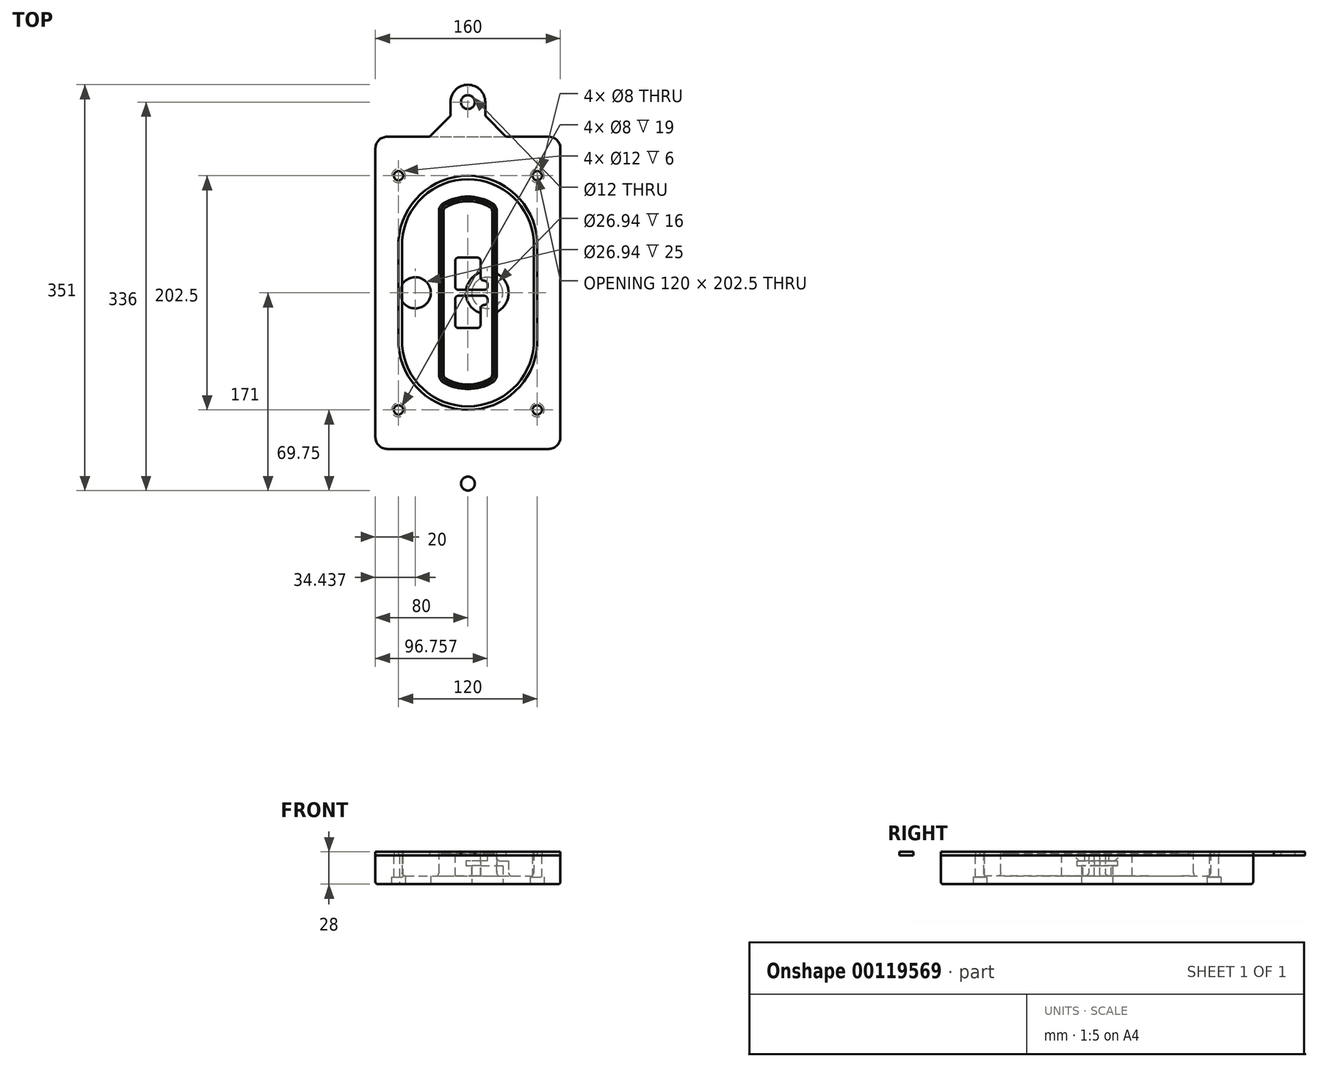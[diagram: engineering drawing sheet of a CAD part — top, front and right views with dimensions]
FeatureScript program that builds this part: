
annotation { "Feature Type Name" : "Feature", "Feature Type Description" : "" }
export const myFeature = defineFeature(function(context is Context, id is Id, definition is map)
    precondition{}
    {
        {
            var Q0;
            Q0=qCreatedBy(makeId("Top.planeOp"),FACE);
            var sketch = newSketch(context, id + "F0", { "sketchPlane" : qUnion([Q0])});
            skPoint(sketch, "E0.rect.middle", {"position": v(0, 0) * mm});
            skLineSegment(sketch, "E1.bottom", {"start": v(-70, -135) * mm, "end": v(70, -135) * mm});
            skLineSegment(sketch, "E1.top", {"start": v(-70, 135) * mm, "end": v(70, 135) * mm});
            skLineSegment(sketch, "E1.left", {"start": v(-80, -125) * mm, "end": v(-80, 125) * mm});
            skLineSegment(sketch, "E1.right", {"start": v(80, -125) * mm, "end": v(80, 125) * mm});
            skLineSegment(sketch, "E2", {"start": v(-80, 135) * mm, "end": v(80, -135) * mm, "construction": true});
            skLineSegment(sketch, "E3", {"start": v(80, 135) * mm, "end": v(-80, -135) * mm, "construction": true});
            skCircle(sketch, "E4", {"center": v(-60, 101.25) * mm, "radius": 4 * mm});
            skCircle(sketch, "E5", {"center": v(60, 101.25) * mm, "radius": 4 * mm});
            skCircle(sketch, "E6", {"center": v(60, -101.25) * mm, "radius": 4 * mm});
            skCircle(sketch, "E7", {"center": v(-60, -101.25) * mm, "radius": 4 * mm});
            skLineSegment(sketch, "E8", {"start": v(-60, 101.25) * mm, "end": v(60, 101.25) * mm, "construction": true});
            skLineSegment(sketch, "E9", {"start": v(60, 101.25) * mm, "end": v(60, -101.25) * mm, "construction": true});
            skLineSegment(sketch, "E10", {"start": v(60, -101.25) * mm, "end": v(-60, -101.25) * mm, "construction": true});
            skLineSegment(sketch, "E11", {"start": v(-60, -101.25) * mm, "end": v(-60, 101.25) * mm, "construction": true});
            skLineSegment(sketch, "E12", {"start": v(-60, 44.66) * mm, "end": v(-60, -44.66) * mm});
            skLineSegment(sketch, "E13", {"start": v(60, 44.66) * mm, "end": v(60, -44.66) * mm});
            skArc(sketch, "E14", {"start": v(59.98, 45.37) * mm, "mid": v(0, 101.25) * mm, "end": v(-59.98, 45.37) * mm});
            skArc(sketch, "E15", {"start": v(-59.98, -45.37) * mm, "mid": v(0, -101.25) * mm, "end": v(59.98, -45.37) * mm});
            skLineSegment(sketch, "E16", {"start": v(-60, 0) * mm, "end": v(60, 0) * mm, "construction": true});
            skPoint(sketch, "E17.visualSharp", {"position": v(-60, -45) * mm});
            skArc(sketch, "E17.filletArc", {"start": v(-60, -44.66) * mm, "mid": v(-60, -45.02) * mm, "end": v(-59.98, -45.37) * mm});
            skPoint(sketch, "E18.visualSharp", {"position": v(-60, 45) * mm});
            skArc(sketch, "E18.filletArc", {"start": v(-59.98, 45.37) * mm, "mid": v(-60, 45.02) * mm, "end": v(-60, 44.66) * mm});
            skPoint(sketch, "E19.visualSharp", {"position": v(60, 45) * mm});
            skArc(sketch, "E19.filletArc", {"start": v(60, 44.66) * mm, "mid": v(60, 45.02) * mm, "end": v(59.98, 45.37) * mm});
            skPoint(sketch, "E20.visualSharp", {"position": v(60, -45) * mm});
            skArc(sketch, "E20.filletArc", {"start": v(59.98, -45.37) * mm, "mid": v(60, -45.02) * mm, "end": v(60, -44.66) * mm});
            skPoint(sketch, "E21.visualSharp", {"position": v(-80, 135) * mm});
            skArc(sketch, "E21.filletArc", {"start": v(-70, 135) * mm, "mid": v(-77.07, 132.07) * mm, "end": v(-80, 125) * mm});
            skPoint(sketch, "E22.visualSharp", {"position": v(80, 135) * mm});
            skArc(sketch, "E22.filletArc", {"start": v(80, 125) * mm, "mid": v(77.07, 132.07) * mm, "end": v(70, 135) * mm});
            skPoint(sketch, "E23.visualSharp", {"position": v(80, -135) * mm});
            skArc(sketch, "E23.filletArc", {"start": v(70, -135) * mm, "mid": v(77.07, -132.07) * mm, "end": v(80, -125) * mm});
            skPoint(sketch, "E24.visualSharp", {"position": v(-80, -135) * mm});
            skArc(sketch, "E24.filletArc", {"start": v(-80, -125) * mm, "mid": v(-77.07, -132.07) * mm, "end": v(-70, -135) * mm});
            skArc(sketch, "E25.0", {"start": v(57, 44.66) * mm, "mid": v(57, 44.9) * mm, "end": v(56.98, 45.16) * mm});
            skLineSegment(sketch, "E25.1", {"start": v(57, 44.66) * mm, "end": v(57, -44.66) * mm});
            skArc(sketch, "E25.2", {"start": v(56.98, -45.16) * mm, "mid": v(57, -44.9) * mm, "end": v(57, -44.66) * mm});
            skArc(sketch, "E25.3", {"start": v(-56.98, -45.16) * mm, "mid": v(0, -98.25) * mm, "end": v(56.98, -45.16) * mm});
            skArc(sketch, "E25.4", {"start": v(-57, -44.66) * mm, "mid": v(-57, -44.9) * mm, "end": v(-56.98, -45.16) * mm});
            skArc(sketch, "E25.5", {"start": v(56.98, 45.16) * mm, "mid": v(0, 98.25) * mm, "end": v(-56.98, 45.16) * mm});
            skLineSegment(sketch, "E25.6", {"start": v(-57, 44.66) * mm, "end": v(-57, -44.66) * mm});
            skArc(sketch, "E25.7", {"start": v(-56.98, 45.16) * mm, "mid": v(-57, 44.9) * mm, "end": v(-57, 44.66) * mm});
            skArc(sketch, "E26.0", {"start": v(-63.97, 45.65) * mm, "mid": v(-64, 45.16) * mm, "end": v(-64, 44.66) * mm});
            skArc(sketch, "E26.1", {"start": v(63.97, 45.65) * mm, "mid": v(0, 105.25) * mm, "end": v(-63.97, 45.65) * mm});
            skArc(sketch, "E26.2", {"start": v(64, 44.66) * mm, "mid": v(64, 45.16) * mm, "end": v(63.97, 45.65) * mm});
            skLineSegment(sketch, "E26.3", {"start": v(64, 44.66) * mm, "end": v(64, -44.66) * mm});
            skArc(sketch, "E26.4", {"start": v(63.97, -45.65) * mm, "mid": v(64, -45.16) * mm, "end": v(64, -44.66) * mm});
            skLineSegment(sketch, "E26.5", {"start": v(-64, 44.66) * mm, "end": v(-64, -44.66) * mm});
            skArc(sketch, "E26.6", {"start": v(-63.97, -45.65) * mm, "mid": v(0, -105.25) * mm, "end": v(63.97, -45.65) * mm});
            skArc(sketch, "E26.7", {"start": v(-64, -44.66) * mm, "mid": v(-64, -45.16) * mm, "end": v(-63.97, -45.65) * mm});
            skSolve(sketch);
        }
        {
            var Q0;
            Q0=makeQuery(id+"F0.imprint","IMPRINT",FACE,{"disambiguationData":[TD([[makeQuery(id+"F0.imprint","IMPRINT",EDGE,{"derivedFrom":sQuery(id+"F0.wireOp",EDGE,"E1.bottom")}),1.0]])]});
            var Q1;
            Q1=makeQuery(id+"F0.imprint","IMPRINT",FACE,{"disambiguationData":[TD([[makeQuery(id+"F0.imprint","IMPRINT",EDGE,{"derivedFrom":sQuery(id+"F0.wireOp",EDGE,"E12")}),1.0]])]});
            var Q2;
            Q2=makeQuery(id+"F0.imprint","IMPRINT",FACE,{"disambiguationData":[TD([[makeQuery(id+"F0.imprint","IMPRINT",EDGE,{"derivedFrom":sQuery(id+"F0.wireOp",EDGE,"E25.0")}),1.0]])]});
            var Q3;
            Q3=makeQuery(id+"F0.imprint","IMPRINT",FACE,{"disambiguationData":[TD([[makeQuery(id+"F0.imprint","IMPRINT",EDGE,{"derivedFrom":sQuery(id+"F0.wireOp",EDGE,"E12")}),-1.0]])]});
            extrude(context, id + "F1", {"entities" : qUnion([Q0, Q1, Q2, Q3]), "oppositeDirection" : true, "depth" : 25 * mm});
        }
        {
            var Q0;
            Q0=makeQuery(id+"F0.imprint","IMPRINT",FACE,{"disambiguationData":[TD([[makeQuery(id+"F0.imprint","IMPRINT",EDGE,{"derivedFrom":sQuery(id+"F0.wireOp",EDGE,"E12")}),1.0]])]});
            extrude(context, id + "F2", {"entities" : qUnion([Q0]), "operationType" : NewBodyOperationType.ADD, "depth" : 3 * mm});
        }
        {
            var Q0;
            Q0=makeQuery(id+"F0.imprint","IMPRINT",FACE,{"disambiguationData":[TD([[makeQuery(id+"F0.imprint","IMPRINT",EDGE,{"derivedFrom":sQuery(id+"F0.wireOp",EDGE,"E25.0")}),1.0]])]});
            extrude(context, id + "F3", {"entities" : qUnion([Q0]), "operationType" : NewBodyOperationType.REMOVE, "oppositeDirection" : true, "depth" : 18 * mm});
        }
        {
            var Q0;
            Q0=makeQuery(id+"F2.opExtrude","CAP_FACE",FACE,{"disambiguationData":[OSD([sQuery(id+"F0.wireOp",EDGE,"E12"),sQuery(id+"F0.wireOp",EDGE,"E13"),sQuery(id+"F0.wireOp",EDGE,"E14"),sQuery(id+"F0.wireOp",EDGE,"E15"),sQuery(id+"F0.wireOp",EDGE,"E17.filletArc"),sQuery(id+"F0.wireOp",EDGE,"E18.filletArc"),sQuery(id+"F0.wireOp",EDGE,"E19.filletArc"),sQuery(id+"F0.wireOp",EDGE,"E20.filletArc"),sQuery(id+"F0.wireOp",EDGE,"E25.0"),sQuery(id+"F0.wireOp",EDGE,"E25.1"),sQuery(id+"F0.wireOp",EDGE,"E25.2"),sQuery(id+"F0.wireOp",EDGE,"E25.3"),sQuery(id+"F0.wireOp",EDGE,"E25.4"),sQuery(id+"F0.wireOp",EDGE,"E25.5"),sQuery(id+"F0.wireOp",EDGE,"E25.6"),sQuery(id+"F0.wireOp",EDGE,"E25.7")])],"isStart":false});
            var sketch = newSketch(context, id + "F4", { "sketchPlane" : qUnion([Q0])});
            skArc(sketch, "E27.0", {"start": v(-20.99, -77.65) * mm, "mid": v(0, -83.25) * mm, "end": v(20.99, -77.65) * mm});
            skArc(sketch, "E28.0", {"start": v(20.99, 77.65) * mm, "mid": v(0, 83.25) * mm, "end": v(-20.99, 77.65) * mm});
            skLineSegment(sketch, "E29", {"start": v(-25, 70.71) * mm, "end": v(-25, -70.71) * mm});
            skLineSegment(sketch, "E30", {"start": v(25, 70.71) * mm, "end": v(25, -70.71) * mm});
            skLineSegment(sketch, "E31", {"start": v(-25, 75.03) * mm, "end": v(25, 75.03) * mm, "construction": true});
            skLineSegment(sketch, "E32", {"start": v(-25, -75.03) * mm, "end": v(25, -75.03) * mm, "construction": true});
            skPoint(sketch, "E33.visualSharp", {"position": v(-25, 75.03) * mm});
            skArc(sketch, "E33.filletArc", {"start": v(-20.99, 77.65) * mm, "mid": v(-23.92, 74.72) * mm, "end": v(-25, 70.71) * mm});
            skPoint(sketch, "E34.visualSharp", {"position": v(25, 75.03) * mm});
            skArc(sketch, "E34.filletArc", {"start": v(25, 70.71) * mm, "mid": v(23.92, 74.72) * mm, "end": v(20.99, 77.65) * mm});
            skPoint(sketch, "E35.visualSharp", {"position": v(25, -75.03) * mm});
            skArc(sketch, "E35.filletArc", {"start": v(20.99, -77.65) * mm, "mid": v(23.92, -74.72) * mm, "end": v(25, -70.71) * mm});
            skPoint(sketch, "E36.visualSharp", {"position": v(-25, -75.03) * mm});
            skArc(sketch, "E36.filletArc", {"start": v(-25, -70.71) * mm, "mid": v(-23.92, -74.72) * mm, "end": v(-20.99, -77.65) * mm});
            skArc(sketch, "E37.0", {"start": v(56.98, 45.16) * mm, "mid": v(0, 98.25) * mm, "end": v(-56.98, 45.16) * mm});
            skArc(sketch, "E37.1", {"start": v(-56.98, 45.16) * mm, "mid": v(-57, 44.9) * mm, "end": v(-57, 44.66) * mm});
            skLineSegment(sketch, "E37.2", {"start": v(-57, 44.66) * mm, "end": v(-57, -44.66) * mm});
            skArc(sketch, "E37.3", {"start": v(-57, -44.66) * mm, "mid": v(-57, -44.9) * mm, "end": v(-56.98, -45.16) * mm});
            skArc(sketch, "E37.4", {"start": v(-56.98, -45.16) * mm, "mid": v(0, -98.25) * mm, "end": v(56.98, -45.16) * mm});
            skArc(sketch, "E37.5", {"start": v(56.98, -45.16) * mm, "mid": v(57, -44.9) * mm, "end": v(57, -44.66) * mm});
            skLineSegment(sketch, "E37.6", {"start": v(57, 44.66) * mm, "end": v(57, -44.66) * mm});
            skArc(sketch, "E37.7", {"start": v(57, 44.66) * mm, "mid": v(57, 44.9) * mm, "end": v(56.98, 45.16) * mm});
            skLineSegment(sketch, "E38.0", {"start": v(23, 70.71) * mm, "end": v(23, -70.71) * mm});
            skArc(sketch, "E38.1", {"start": v(19.99, -75.92) * mm, "mid": v(22.2, -73.72) * mm, "end": v(23, -70.71) * mm});
            skArc(sketch, "E38.2", {"start": v(-19.99, -75.92) * mm, "mid": v(0, -81.25) * mm, "end": v(19.99, -75.92) * mm});
            skArc(sketch, "E38.3", {"start": v(-23, -70.71) * mm, "mid": v(-22.2, -73.72) * mm, "end": v(-19.99, -75.92) * mm});
            skLineSegment(sketch, "E38.4", {"start": v(-23, 70.71) * mm, "end": v(-23, -70.71) * mm});
            skArc(sketch, "E38.5", {"start": v(23, 70.71) * mm, "mid": v(22.2, 73.72) * mm, "end": v(19.99, 75.92) * mm});
            skArc(sketch, "E38.6", {"start": v(-19.99, 75.92) * mm, "mid": v(-22.2, 73.72) * mm, "end": v(-23, 70.71) * mm});
            skArc(sketch, "E38.7", {"start": v(19.99, 75.92) * mm, "mid": v(0, 81.25) * mm, "end": v(-19.99, 75.92) * mm});
            skArc(sketch, "E39.0", {"start": v(21, 70.71) * mm, "mid": v(20.46, 72.72) * mm, "end": v(19, 74.18) * mm});
            skLineSegment(sketch, "E39.1", {"start": v(21, 70.71) * mm, "end": v(21, -70.71) * mm});
            skArc(sketch, "E39.2", {"start": v(19, -74.18) * mm, "mid": v(20.46, -72.72) * mm, "end": v(21, -70.71) * mm});
            skArc(sketch, "E39.3", {"start": v(-19, -74.18) * mm, "mid": v(0, -79.25) * mm, "end": v(19, -74.18) * mm});
            skArc(sketch, "E39.4", {"start": v(-21, -70.71) * mm, "mid": v(-20.46, -72.72) * mm, "end": v(-19, -74.18) * mm});
            skArc(sketch, "E39.5", {"start": v(19, 74.18) * mm, "mid": v(0, 79.25) * mm, "end": v(-19, 74.18) * mm});
            skLineSegment(sketch, "E39.6", {"start": v(-21, 70.71) * mm, "end": v(-21, -70.71) * mm});
            skArc(sketch, "E39.7", {"start": v(-19, 74.18) * mm, "mid": v(-20.46, 72.72) * mm, "end": v(-21, 70.71) * mm});
            skLineSegment(sketch, "E40", {"start": v(-25, 0) * mm, "end": v(25, 0) * mm, "construction": true});
            skLineSegment(sketch, "E41", {"start": v(-11, 5.5) * mm, "end": v(-11, 27.5) * mm});
            skLineSegment(sketch, "E42", {"start": v(-8, 30.5) * mm, "end": v(8, 30.5) * mm});
            skLineSegment(sketch, "E43", {"start": v(11, 27.5) * mm, "end": v(11, 13.5) * mm});
            skLineSegment(sketch, "E44", {"start": v(14, 10.5) * mm, "end": v(14, 10.5) * mm});
            skLineSegment(sketch, "E45", {"start": v(17, 7.5) * mm, "end": v(17, 5.5) * mm});
            skLineSegment(sketch, "E46", {"start": v(14, 2.5) * mm, "end": v(-8, 2.5) * mm});
            skPoint(sketch, "E47.visualSharp", {"position": v(-11, 30.5) * mm});
            skArc(sketch, "E47.filletArc", {"start": v(-8, 30.5) * mm, "mid": v(-10.12, 29.62) * mm, "end": v(-11, 27.5) * mm});
            skPoint(sketch, "E48.visualSharp", {"position": v(11, 30.5) * mm});
            skArc(sketch, "E48.filletArc", {"start": v(11, 27.5) * mm, "mid": v(10.12, 29.62) * mm, "end": v(8, 30.5) * mm});
            skPoint(sketch, "E49.visualSharp", {"position": v(11, 10.5) * mm});
            skArc(sketch, "E49.filletArc", {"start": v(11, 13.5) * mm, "mid": v(11.88, 11.38) * mm, "end": v(14, 10.5) * mm});
            skPoint(sketch, "E50.visualSharp", {"position": v(17, 10.5) * mm});
            skArc(sketch, "E50.filletArc", {"start": v(17, 7.5) * mm, "mid": v(16.12, 9.62) * mm, "end": v(14, 10.5) * mm});
            skPoint(sketch, "E51.visualSharp", {"position": v(17, 2.5) * mm});
            skArc(sketch, "E51.filletArc", {"start": v(14, 2.5) * mm, "mid": v(16.12, 3.38) * mm, "end": v(17, 5.5) * mm});
            skPoint(sketch, "E52.visualSharp", {"position": v(-11, 2.5) * mm});
            skArc(sketch, "E52.filletArc", {"start": v(-11, 5.5) * mm, "mid": v(-10.12, 3.38) * mm, "end": v(-8, 2.5) * mm});
            skLineSegment(sketch, "E53.0.MirrorCS", {"start": v(14, -2.5) * mm, "end": v(-8, -2.5) * mm});
            skArc(sketch, "E54.0.MirrorCS", {"start": v(-11, -5.5) * mm, "mid": v(-10.12, -3.38) * mm, "end": v(-8, -2.5) * mm});
            skLineSegment(sketch, "E55.0.MirrorCS", {"start": v(-11, -5.5) * mm, "end": v(-11, -27.5) * mm});
            skArc(sketch, "E56.0.MirrorCS", {"start": v(-8, -30.5) * mm, "mid": v(-10.12, -29.62) * mm, "end": v(-11, -27.5) * mm});
            skLineSegment(sketch, "E57.0.MirrorCS", {"start": v(-8, -30.5) * mm, "end": v(8, -30.5) * mm});
            skArc(sketch, "E58.0.MirrorCS", {"start": v(11, -27.5) * mm, "mid": v(10.12, -29.62) * mm, "end": v(8, -30.5) * mm});
            skLineSegment(sketch, "E59.0.MirrorCS", {"start": v(11, -27.5) * mm, "end": v(11, -13.5) * mm});
            skArc(sketch, "E60.0.MirrorCS", {"start": v(11, -13.5) * mm, "mid": v(11.88, -11.38) * mm, "end": v(14, -10.5) * mm});
            skArc(sketch, "E61.0.MirrorCS", {"start": v(17, -7.5) * mm, "mid": v(16.12, -9.62) * mm, "end": v(14, -10.5) * mm});
            skLineSegment(sketch, "E62.0.MirrorCS", {"start": v(17, -7.5) * mm, "end": v(17, -5.5) * mm});
            skArc(sketch, "E63.0.MirrorCS", {"start": v(14, -2.5) * mm, "mid": v(16.12, -3.38) * mm, "end": v(17, -5.5) * mm});
            skSolve(sketch);
        }
        {
            var Q0;
            Q0=makeQuery(id+"F4.imprint","IMPRINT",FACE,{"disambiguationData":[TD([[makeQuery(id+"F4.imprint","IMPRINT",EDGE,{"derivedFrom":sQuery(id+"F4.wireOp",EDGE,"E27.0")}),1.0]])]});
            var Q1;
            Q1=makeQuery(id+"F4.imprint","IMPRINT",FACE,{"disambiguationData":[TD([[makeQuery(id+"F4.imprint","IMPRINT",EDGE,{"derivedFrom":sQuery(id+"F4.wireOp",EDGE,"E38.0")}),-1.0]])]});
            var Q2;
            Q2=makeQuery(id+"F4.imprint","IMPRINT",FACE,{"disambiguationData":[TD([[makeQuery(id+"F4.imprint","IMPRINT",EDGE,{"derivedFrom":sQuery(id+"F4.wireOp",EDGE,"E39.0")}),1.0]])]});
            extrude(context, id + "F5", {"entities" : qUnion([Q0, Q1, Q2]), "operationType" : NewBodyOperationType.ADD, "endBound" : BoundingType.UP_TO_NEXT, "oppositeDirection" : true, "depth" : 25 * mm});
        }
        {
            var Q0;
            Q0=makeQuery(id+"F4.imprint","IMPRINT",FACE,{"disambiguationData":[TD([[makeQuery(id+"F4.imprint","IMPRINT",EDGE,{"derivedFrom":sQuery(id+"F4.wireOp",EDGE,"E38.0")}),-1.0]])]});
            extrude(context, id + "F6", {"entities" : qUnion([Q0]), "operationType" : NewBodyOperationType.REMOVE, "oppositeDirection" : true, "depth" : 2 * mm});
        }
        {
            var Q0;
            Q0=makeQuery(id+"F1.opExtrude","CAP_FACE",FACE,{"disambiguationData":[OSD([sQuery(id+"F0.wireOp",EDGE,"E1.bottom"),sQuery(id+"F0.wireOp",EDGE,"E1.top"),sQuery(id+"F0.wireOp",EDGE,"E1.left"),sQuery(id+"F0.wireOp",EDGE,"E1.right"),sQuery(id+"F0.wireOp",EDGE,"E4"),sQuery(id+"F0.wireOp",EDGE,"E5"),sQuery(id+"F0.wireOp",EDGE,"E6"),sQuery(id+"F0.wireOp",EDGE,"E7"),sQuery(id+"F0.wireOp",EDGE,"E21.filletArc"),sQuery(id+"F0.wireOp",EDGE,"E22.filletArc"),sQuery(id+"F0.wireOp",EDGE,"E23.filletArc"),sQuery(id+"F0.wireOp",EDGE,"E24.filletArc")])],"isStart":false});
            var sketch = newSketch(context, id + "F7", { "sketchPlane" : qUnion([Q0])});
            skCircle(sketch, "E64", {"center": v(16.76, 0) * mm, "radius": 13.47 * mm});
            skCircle(sketch, "E65", {"center": v(-45.56, 0) * mm, "radius": 13.47 * mm});
            skLineSegment(sketch, "E66", {"start": v(80, 0) * mm, "end": v(-80, 0) * mm});
            skCircle(sketch, "E67", {"center": v(16.76, 0) * mm, "radius": 18.47 * mm});
            skCircle(sketch, "E68", {"center": v(60, -101.25) * mm, "radius": 6 * mm});
            skCircle(sketch, "E69", {"center": v(-60, -101.25) * mm, "radius": 6 * mm});
            skCircle(sketch, "E70", {"center": v(-60, 101.25) * mm, "radius": 6 * mm});
            skCircle(sketch, "E71", {"center": v(60, 101.25) * mm, "radius": 6 * mm});
            skSolve(sketch);
        }
        {
            var Q0;
            {var subQ1=sQuery(id+"F7.wireOp",EDGE,"E66");var subQ4=sQuery(id+"F7.wireOp",EDGE,"E64");var subQ6=makeQuery(id+"F7.imprint","INTERSECT",VERTEX,{"disambiguationData":[OD(0.0)],"derivedFrom":[subQ4,subQ1]});Q0=makeQuery(id+"F7.imprint","IMPRINT",FACE,{"disambiguationData":[TD([[makeQuery(id+"F7.imprint","IMPRINT",EDGE,{"disambiguationData":[TD([[subQ6,-1.0]])],"derivedFrom":subQ4}),-1.0]])]});}
            var Q1;
            {var subQ0=sQuery(id+"F7.wireOp",EDGE,"E66");var subQ1=sQuery(id+"F7.wireOp",EDGE,"E64");var subQ3=makeQuery(id+"F7.imprint","INTERSECT",VERTEX,{"disambiguationData":[OD(0.0)],"derivedFrom":[subQ1,subQ0]});Q1=makeQuery(id+"F7.imprint","IMPRINT",FACE,{"disambiguationData":[TD([[makeQuery(id+"F7.imprint","IMPRINT",EDGE,{"disambiguationData":[TD([[subQ3,-1.0]])],"derivedFrom":subQ1}),1.0]])]});}
            var Q2;
            {var subQ0=sQuery(id+"F7.wireOp",EDGE,"E66");var subQ1=sQuery(id+"F7.wireOp",EDGE,"E64");var subQ3=makeQuery(id+"F7.imprint","INTERSECT",VERTEX,{"disambiguationData":[OD(0.0)],"derivedFrom":[subQ1,subQ0]});Q2=makeQuery(id+"F7.imprint","IMPRINT",FACE,{"disambiguationData":[TD([[makeQuery(id+"F7.imprint","IMPRINT",EDGE,{"disambiguationData":[TD([[subQ3,1.0]])],"derivedFrom":subQ1}),1.0]])]});}
            var Q3;
            {var subQ1=sQuery(id+"F7.wireOp",EDGE,"E66");var subQ4=sQuery(id+"F7.wireOp",EDGE,"E64");var subQ6=makeQuery(id+"F7.imprint","INTERSECT",VERTEX,{"disambiguationData":[OD(0.0)],"derivedFrom":[subQ4,subQ1]});Q3=makeQuery(id+"F7.imprint","IMPRINT",FACE,{"disambiguationData":[TD([[makeQuery(id+"F7.imprint","IMPRINT",EDGE,{"disambiguationData":[TD([[subQ6,1.0]])],"derivedFrom":subQ4}),-1.0]])]});}
            extrude(context, id + "F8", {"entities" : qUnion([Q0, Q1, Q2, Q3]), "operationType" : NewBodyOperationType.ADD, "oppositeDirection" : true, "depth" : 20 * mm});
        }
        {
            var Q0;
            {var subQ0=sQuery(id+"F7.wireOp",EDGE,"E66");var subQ1=sQuery(id+"F7.wireOp",EDGE,"E64");var subQ3=makeQuery(id+"F7.imprint","INTERSECT",VERTEX,{"disambiguationData":[OD(0.0)],"derivedFrom":[subQ1,subQ0]});Q0=makeQuery(id+"F7.imprint","IMPRINT",FACE,{"disambiguationData":[TD([[makeQuery(id+"F7.imprint","IMPRINT",EDGE,{"disambiguationData":[TD([[subQ3,-1.0]])],"derivedFrom":subQ1}),1.0]])]});}
            var Q1;
            {var subQ0=sQuery(id+"F7.wireOp",EDGE,"E66");var subQ1=sQuery(id+"F7.wireOp",EDGE,"E64");var subQ3=makeQuery(id+"F7.imprint","INTERSECT",VERTEX,{"disambiguationData":[OD(0.0)],"derivedFrom":[subQ1,subQ0]});Q1=makeQuery(id+"F7.imprint","IMPRINT",FACE,{"disambiguationData":[TD([[makeQuery(id+"F7.imprint","IMPRINT",EDGE,{"disambiguationData":[TD([[subQ3,1.0]])],"derivedFrom":subQ1}),1.0]])]});}
            extrude(context, id + "F9", {"entities" : qUnion([Q0, Q1]), "operationType" : NewBodyOperationType.REMOVE, "oppositeDirection" : true, "depth" : 16 * mm});
        }
        {
            var Q0;
            {var subQ0=sQuery(id+"F7.wireOp",EDGE,"E66");var subQ1=sQuery(id+"F7.wireOp",EDGE,"E65");var subQ3=makeQuery(id+"F7.imprint","INTERSECT",VERTEX,{"disambiguationData":[OD(0.0)],"derivedFrom":[subQ1,subQ0]});Q0=makeQuery(id+"F7.imprint","IMPRINT",FACE,{"disambiguationData":[TD([[makeQuery(id+"F7.imprint","IMPRINT",EDGE,{"disambiguationData":[TD([[subQ3,-1.0]])],"derivedFrom":subQ1}),1.0]])]});}
            var Q1;
            {var subQ0=sQuery(id+"F7.wireOp",EDGE,"E66");var subQ1=sQuery(id+"F7.wireOp",EDGE,"E65");var subQ3=makeQuery(id+"F7.imprint","INTERSECT",VERTEX,{"disambiguationData":[OD(0.0)],"derivedFrom":[subQ1,subQ0]});Q1=makeQuery(id+"F7.imprint","IMPRINT",FACE,{"disambiguationData":[TD([[makeQuery(id+"F7.imprint","IMPRINT",EDGE,{"disambiguationData":[TD([[subQ3,1.0]])],"derivedFrom":subQ1}),1.0]])]});}
            extrude(context, id + "F10", {"entities" : qUnion([Q0, Q1]), "operationType" : NewBodyOperationType.REMOVE, "oppositeDirection" : true, "depth" : 25 * mm});
        }
        {
            var Q0;
            Q0=makeQuery(id+"F7.imprint","IMPRINT",FACE,{"disambiguationData":[TD([[makeQuery(id+"F7.imprint","IMPRINT",EDGE,{"derivedFrom":sQuery(id+"F7.wireOp",EDGE,"E68")}),1.0]])]});
            var Q1;
            Q1=makeQuery(id+"F7.imprint","IMPRINT",FACE,{"disambiguationData":[TD([[makeQuery(id+"F7.imprint","IMPRINT",EDGE,{"derivedFrom":makeQuery(id+"F1.opExtrude","CAP_EDGE",EDGE,{"disambiguationData":[OSD([sQuery(id+"F0.wireOp",EDGE,"E5")])],"isStart":false})}),-1.0]])]});
            var Q2;
            Q2=makeQuery(id+"F7.imprint","IMPRINT",FACE,{"disambiguationData":[TD([[makeQuery(id+"F7.imprint","IMPRINT",EDGE,{"derivedFrom":sQuery(id+"F7.wireOp",EDGE,"E69")}),1.0]])]});
            var Q3;
            Q3=makeQuery(id+"F7.imprint","IMPRINT",FACE,{"disambiguationData":[TD([[makeQuery(id+"F7.imprint","IMPRINT",EDGE,{"derivedFrom":makeQuery(id+"F1.opExtrude","CAP_EDGE",EDGE,{"disambiguationData":[OSD([sQuery(id+"F0.wireOp",EDGE,"E4")])],"isStart":false})}),-1.0]])]});
            var Q4;
            Q4=makeQuery(id+"F7.imprint","IMPRINT",FACE,{"disambiguationData":[TD([[makeQuery(id+"F7.imprint","IMPRINT",EDGE,{"derivedFrom":sQuery(id+"F7.wireOp",EDGE,"E70")}),1.0]])]});
            var Q5;
            Q5=makeQuery(id+"F7.imprint","IMPRINT",FACE,{"disambiguationData":[TD([[makeQuery(id+"F7.imprint","IMPRINT",EDGE,{"derivedFrom":makeQuery(id+"F1.opExtrude","CAP_EDGE",EDGE,{"disambiguationData":[OSD([sQuery(id+"F0.wireOp",EDGE,"E7")])],"isStart":false})}),-1.0]])]});
            var Q6;
            Q6=makeQuery(id+"F7.imprint","IMPRINT",FACE,{"disambiguationData":[TD([[makeQuery(id+"F7.imprint","IMPRINT",EDGE,{"derivedFrom":sQuery(id+"F7.wireOp",EDGE,"E71")}),1.0]])]});
            var Q7;
            Q7=makeQuery(id+"F7.imprint","IMPRINT",FACE,{"disambiguationData":[TD([[makeQuery(id+"F7.imprint","IMPRINT",EDGE,{"derivedFrom":makeQuery(id+"F1.opExtrude","CAP_EDGE",EDGE,{"disambiguationData":[OSD([sQuery(id+"F0.wireOp",EDGE,"E6")])],"isStart":false})}),-1.0]])]});
            extrude(context, id + "F11", {"entities" : qUnion([Q0, Q1, Q2, Q3, Q4, Q5, Q6, Q7]), "operationType" : NewBodyOperationType.REMOVE, "oppositeDirection" : true, "depth" : 6 * mm});
        }
        {
            var Q0;
            Q0=makeQuery(id+"F9.boolean.opBoolean","COPY",FACE,{"derivedFrom":makeQuery(id+"F9.opExtrude","CAP_FACE",FACE,{"disambiguationData":[OSD([sQuery(id+"F7.wireOp",EDGE,"E64")])],"isStart":false})});
            var sketch = newSketch(context, id + "F12", { "sketchPlane" : qUnion([Q0])});
            skArc(sketch, "E72.0", {"start": v(11, 17.55) * mm, "mid": v(2.57, 11.82) * mm, "end": v(-1.54, 2.5) * mm});
            skArc(sketch, "E72.1", {"start": v(-1.54, -2.5) * mm, "mid": v(2.57, -11.82) * mm, "end": v(11, -17.55) * mm});
            skLineSegment(sketch, "E73", {"start": v(-1.54, -2.5) * mm, "end": v(14, -2.5) * mm});
            skLineSegment(sketch, "E74.0", {"start": v(14, 2.5) * mm, "end": v(-1.54, 2.5) * mm});
            skArc(sketch, "E74.1", {"start": v(14, 2.5) * mm, "mid": v(16.12, 3.38) * mm, "end": v(17, 5.5) * mm});
            skLineSegment(sketch, "E74.2", {"start": v(17, 7.5) * mm, "end": v(17, 5.5) * mm});
            skArc(sketch, "E74.3", {"start": v(17, 7.5) * mm, "mid": v(16.12, 9.62) * mm, "end": v(14, 10.5) * mm});
            skArc(sketch, "E74.4", {"start": v(11, 13.5) * mm, "mid": v(11.88, 11.38) * mm, "end": v(14, 10.5) * mm});
            skLineSegment(sketch, "E74.5", {"start": v(11, 17.55) * mm, "end": v(11, 13.5) * mm});
            skLineSegment(sketch, "E74.7", {"start": v(14, -2.5) * mm, "end": v(-1.54, -2.5) * mm});
            skArc(sketch, "E74.8", {"start": v(14, -2.5) * mm, "mid": v(16.12, -3.38) * mm, "end": v(17, -5.5) * mm});
            skLineSegment(sketch, "E74.9", {"start": v(17, -7.5) * mm, "end": v(17, -5.5) * mm});
            skArc(sketch, "E74.10", {"start": v(17, -7.5) * mm, "mid": v(16.12, -9.62) * mm, "end": v(14, -10.5) * mm});
            skArc(sketch, "E74.11", {"start": v(11, -13.5) * mm, "mid": v(11.88, -11.38) * mm, "end": v(14, -10.5) * mm});
            skLineSegment(sketch, "E74.12", {"start": v(11, -17.55) * mm, "end": v(11, -13.5) * mm});
            skPoint(sketch, "E75.orphan", {"position": v(11, -27.5) * mm});
            skPoint(sketch, "E76.orphan", {"position": v(-8, -2.5) * mm});
            skPoint(sketch, "E77.orphan", {"position": v(-8, 2.5) * mm});
            skPoint(sketch, "E78.orphan", {"position": v(11, 27.5) * mm});
            skSolve(sketch);
        }
        {
            var Q0;
            {var subQ7=sQuery(id+"F12.wireOp",EDGE,"E72.0");var subQ14=sQuery(id+"F12.wireOp",EDGE,"E72.1");var subQ16=sQuery(id+"F12.wireOp",EDGE,"E74.1");var subQ18=sQuery(id+"F12.wireOp",EDGE,"E74.8");Q0=qUnion([makeQuery(id+"F12.imprint","IMPRINT",FACE,{"disambiguationData":[TD([[makeQuery(id+"F12.imprint","IMPRINT",EDGE,{"derivedFrom":subQ7}),1.0]])]}),makeQuery(id+"F12.imprint","IMPRINT",FACE,{"disambiguationData":[TD([[makeQuery(id+"F12.imprint","IMPRINT",EDGE,{"derivedFrom":subQ14}),1.0]])]}),makeQuery(id+"F12.imprint","IMPRINT",FACE,{"disambiguationData":[TD([[makeQuery(id+"F12.imprint","IMPRINT",EDGE,{"derivedFrom":subQ16}),1.0]])]}),makeQuery(id+"F12.imprint","IMPRINT",FACE,{"disambiguationData":[TD([[makeQuery(id+"F12.imprint","IMPRINT",EDGE,{"derivedFrom":subQ18}),-1.0]])]})]);}
            var Q1;
            Q1=makeQuery(id+"F5.boolean.opBoolean","SPLIT",FACE,{"disambiguationData":[TD([makeQuery(id+"F5.opExtrude","SWEPT_FACE",FACE,{"disambiguationData":[OSD([sQuery(id+"F4.wireOp",EDGE,"E41")])]})])],"derivedFrom":makeQuery(id+"F3.boolean.opBoolean","COPY",FACE,{"derivedFrom":makeQuery(id+"F3.opExtrude","CAP_FACE",FACE,{"disambiguationData":[OSD([sQuery(id+"F0.wireOp",EDGE,"E25.0"),sQuery(id+"F0.wireOp",EDGE,"E25.1"),sQuery(id+"F0.wireOp",EDGE,"E25.2"),sQuery(id+"F0.wireOp",EDGE,"E25.3"),sQuery(id+"F0.wireOp",EDGE,"E25.4"),sQuery(id+"F0.wireOp",EDGE,"E25.5"),sQuery(id+"F0.wireOp",EDGE,"E25.6"),sQuery(id+"F0.wireOp",EDGE,"E25.7")])],"isStart":false})})});
            extrude(context, id + "F13", {"entities" : qUnion([Q0]), "operationType" : NewBodyOperationType.REMOVE, "endBound" : BoundingType.UP_TO_SURFACE, "endBoundEntityFace" : qUnion([Q1]), "depth" : 25 * mm});
        }
        {
            var Q0;
            Q0=makeQuery(id+"F3.boolean.opBoolean","COPY",EDGE,{"derivedFrom":makeQuery(id+"F3.opExtrude","CAP_EDGE",EDGE,{"disambiguationData":[OSD([sQuery(id+"F0.wireOp",EDGE,"E25.6")])],"isStart":false})});
            var Q1;
            Q1=makeQuery(id+"F8.boolean.opBoolean","INTERSECT",EDGE,{"derivedFrom":[makeQuery(id+"F5.opExtrude","SWEPT_FACE",FACE,{"disambiguationData":[OSD([sQuery(id+"F4.wireOp",EDGE,"E30")])]}),makeQuery(id+"F8.opExtrude","CAP_FACE",FACE,{"disambiguationData":[OSD([sQuery(id+"F7.wireOp",EDGE,"E67")])],"isStart":false})]});
            var Q2;
            Q2=makeQuery(id+"F8.boolean.opBoolean","INTERSECT",EDGE,{"disambiguationData":[OD(1.0)],"derivedFrom":[makeQuery(id+"F5.opExtrude","SWEPT_FACE",FACE,{"disambiguationData":[OSD([sQuery(id+"F4.wireOp",EDGE,"E30")])]}),makeQuery(id+"F8.opExtrude","SWEPT_FACE",FACE,{"disambiguationData":[OSD([sQuery(id+"F7.wireOp",EDGE,"E67")])]})]});
            var Q3;
            {var subQ0=sQuery(id+"F4.wireOp",EDGE,"E30");Q3=makeQuery(id+"F8.boolean.opBoolean","SPLIT",EDGE,{"disambiguationData":[TD([makeQuery(id+"F5.opExtrude","SWEPT_FACE",FACE,{"disambiguationData":[OSD([sQuery(id+"F4.wireOp",EDGE,"E35.filletArc")])]})])],"derivedFrom":makeQuery(id+"F5.opExtrude","CAP_EDGE",EDGE,{"disambiguationData":[OSD([subQ0])],"isStart":false})});}
            var Q4;
            {var subQ0=sQuery(id+"F0.wireOp",EDGE,"E25.7");var subQ1=sQuery(id+"F0.wireOp",EDGE,"E25.1");var subQ2=sQuery(id+"F0.wireOp",EDGE,"E25.6");var subQ3=sQuery(id+"F0.wireOp",EDGE,"E25.5");var subQ4=sQuery(id+"F0.wireOp",EDGE,"E25.4");var subQ5=sQuery(id+"F0.wireOp",EDGE,"E25.0");var subQ6=sQuery(id+"F0.wireOp",EDGE,"E25.2");var subQ7=sQuery(id+"F0.wireOp",EDGE,"E25.3");Q4=makeQuery(id+"F8.boolean.opBoolean","INTERSECT",EDGE,{"derivedFrom":[makeQuery(id+"F5.boolean.opBoolean","SPLIT",FACE,{"disambiguationData":[TD([makeQuery(id+"F2.opExtrude","SWEPT_FACE",FACE,{"disambiguationData":[OSD([subQ5])]})])],"derivedFrom":makeQuery(id+"F3.boolean.opBoolean","COPY",FACE,{"derivedFrom":makeQuery(id+"F3.opExtrude","CAP_FACE",FACE,{"disambiguationData":[OSD([subQ5,subQ1,subQ6,subQ7,subQ4,subQ3,subQ2,subQ0])],"isStart":false})})}),makeQuery(id+"F8.opExtrude","SWEPT_FACE",FACE,{"disambiguationData":[OSD([sQuery(id+"F7.wireOp",EDGE,"E67")])]})]});}
            var Q5;
            Q5=makeQuery(id+"F8.boolean.opBoolean","INTERSECT",EDGE,{"disambiguationData":[OD(0.0)],"derivedFrom":[makeQuery(id+"F5.opExtrude","SWEPT_FACE",FACE,{"disambiguationData":[OSD([sQuery(id+"F4.wireOp",EDGE,"E30")])]}),makeQuery(id+"F8.opExtrude","SWEPT_FACE",FACE,{"disambiguationData":[OSD([sQuery(id+"F7.wireOp",EDGE,"E67")])]})]});
            fillet(context, id + "F14", {"entities" : qUnion([Q0, Q1, Q2, Q3, Q4, Q5]), "radius" : 3 * mm, "tangentPropagation" : true, "allowEdgeOverflow" : false});
        }
        {
            var Q0;
            Q0=makeQuery(id+"F1.opExtrude","CAP_EDGE",EDGE,{"disambiguationData":[OSD([sQuery(id+"F0.wireOp",EDGE,"E1.bottom")])],"isStart":false});
            fillet(context, id + "F15", {"entities" : qUnion([Q0]), "radius" : 2 * mm, "tangentPropagation" : true, "allowEdgeOverflow" : false});
        }
        {
            var Q0;
            {var subQ0=sQuery(id+"F0.wireOp",EDGE,"E22.filletArc");var subQ1=sQuery(id+"F0.wireOp",EDGE,"E7");var subQ2=sQuery(id+"F0.wireOp",EDGE,"E6");var subQ3=sQuery(id+"F0.wireOp",EDGE,"E5");var subQ4=sQuery(id+"F0.wireOp",EDGE,"E4");var subQ5=sQuery(id+"F0.wireOp",EDGE,"E1.bottom");var subQ6=sQuery(id+"F0.wireOp",EDGE,"E21.filletArc");var subQ7=sQuery(id+"F0.wireOp",EDGE,"E1.top");var subQ8=sQuery(id+"F0.wireOp",EDGE,"E1.left");var subQ9=sQuery(id+"F0.wireOp",EDGE,"E1.right");var subQ10=sQuery(id+"F0.wireOp",EDGE,"E23.filletArc");var subQ11=sQuery(id+"F0.wireOp",EDGE,"E24.filletArc");Q0=makeQuery(id+"F2.boolean.opBoolean","SPLIT",FACE,{"disambiguationData":[TD([makeQuery(id+"F1.opExtrude","SWEPT_FACE",FACE,{"disambiguationData":[OSD([subQ5])]})])],"derivedFrom":makeQuery(id+"F1.opExtrude","CAP_FACE",FACE,{"disambiguationData":[OSD([subQ5,subQ7,subQ8,subQ9,subQ4,subQ3,subQ2,subQ1,subQ6,subQ0,subQ10,subQ11])],"isStart":true})});}
            var sketch = newSketch(context, id + "F16", { "sketchPlane" : qUnion([Q0])});
            skLineSegment(sketch, "E79", {"start": v(0, 135) * mm, "end": v(0, 165) * mm, "construction": true});
            skCircle(sketch, "E80", {"center": v(0, 165) * mm, "radius": 6 * mm});
            skLineSegment(sketch, "E81", {"start": v(-15, 165) * mm, "end": v(-15, 153) * mm});
            skLineSegment(sketch, "E82", {"start": v(-15, 153) * mm, "end": v(-33, 135) * mm});
            skLineSegment(sketch, "E83", {"start": v(15, 165) * mm, "end": v(15, 153) * mm});
            skLineSegment(sketch, "E84", {"start": v(15, 153) * mm, "end": v(33, 135) * mm});
            skArc(sketch, "E85", {"start": v(15, 165) * mm, "mid": v(0, 180) * mm, "end": v(-15, 165) * mm});
            skLineSegment(sketch, "E86", {"start": v(-80, 0) * mm, "end": v(77.84, 0) * mm, "construction": true});
            skPoint(sketch, "E86.endSnap0", {"position": v(60, 0) * mm});
            skCircle(sketch, "E87.MirrorC", {"center": v(0, -165) * mm, "radius": 6 * mm});
            skLineSegment(sketch, "E88.MirrorCS", {"start": v(-15, -165) * mm, "end": v(-15, -153) * mm});
            skLineSegment(sketch, "E89.MirrorCS", {"start": v(15, -165) * mm, "end": v(15, -153) * mm});
            skArc(sketch, "E90.MirrorCS", {"start": v(15, -165) * mm, "mid": v(0, -180) * mm, "end": v(-15, -165) * mm});
            skLineSegment(sketch, "E91.MirrorCS", {"start": v(15, -153) * mm, "end": v(33, -135) * mm});
            skLineSegment(sketch, "E92.MirrorCS", {"start": v(-15, -153) * mm, "end": v(-33, -135) * mm});
            skLineSegment(sketch, "E93.MirrorCS", {"start": v(0, -135) * mm, "end": v(0, -165) * mm, "construction": true});
            skSolve(sketch);
        }
        {
            var Q0;
            Q0=makeQuery(id+"F16.imprint","IMPRINT",FACE,{"disambiguationData":[TD([[makeQuery(id+"F16.imprint","IMPRINT",EDGE,{"derivedFrom":sQuery(id+"F16.wireOp",EDGE,"E87.MirrorC")}),1.0]])]});
            var Q1;
            Q1=makeQuery(id+"F16.imprint","IMPRINT",FACE,{"disambiguationData":[TD([[makeQuery(id+"F16.imprint","IMPRINT",EDGE,{"derivedFrom":sQuery(id+"F16.wireOp",EDGE,"E80")}),-1.0]])]});
            var Q2;
            Q2=makeQuery(id+"F16.imprint","IMPRINT",FACE,{"disambiguationData":[TD([[makeQuery(id+"F16.imprint","IMPRINT",EDGE,{"derivedFrom":makeQuery(id+"F1.opExtrude","CAP_EDGE",EDGE,{"disambiguationData":[OSD([sQuery(id+"F0.wireOp",EDGE,"E1.left")])],"isStart":true})}),-1.0]])]});
            var Q3;
            Q3=makeQuery(id+"F2.opExtrude","CAP_FACE",FACE,{"disambiguationData":[OSD([sQuery(id+"F0.wireOp",EDGE,"E12"),sQuery(id+"F0.wireOp",EDGE,"E13"),sQuery(id+"F0.wireOp",EDGE,"E14"),sQuery(id+"F0.wireOp",EDGE,"E15"),sQuery(id+"F0.wireOp",EDGE,"E17.filletArc"),sQuery(id+"F0.wireOp",EDGE,"E18.filletArc"),sQuery(id+"F0.wireOp",EDGE,"E19.filletArc"),sQuery(id+"F0.wireOp",EDGE,"E20.filletArc"),sQuery(id+"F0.wireOp",EDGE,"E25.0"),sQuery(id+"F0.wireOp",EDGE,"E25.1"),sQuery(id+"F0.wireOp",EDGE,"E25.2"),sQuery(id+"F0.wireOp",EDGE,"E25.3"),sQuery(id+"F0.wireOp",EDGE,"E25.4"),sQuery(id+"F0.wireOp",EDGE,"E25.5"),sQuery(id+"F0.wireOp",EDGE,"E25.6"),sQuery(id+"F0.wireOp",EDGE,"E25.7")])],"isStart":false});
            extrude(context, id + "F17", {"entities" : qUnion([Q0, Q1, Q2]), "endBound" : BoundingType.UP_TO_SURFACE, "endBoundEntityFace" : qUnion([Q3]), "depth" : 25 * mm});
        }
    });
